FCSTD DOCUMENT  (FreeCAD 0.18R15611 (Git))
Label: sqare140mm
License: All rights reserved
LicenseURL: http://en.wikipedia.org/wiki/All_rights_reserved
objects: Sketcher::SketchObject×1, PartDesign::Pad×1, PartDesign::Body×1
note: 4 computed .brp shape members not serialized (recipe doc carries the construction recipe); baked Part::Feature solids carry a one-line shape summary decoded from their .brp

FEATURE [Sketcher::SketchObject] Sketch
  MapMode = 5
  Support = -> [XY_Plane]
  sketch-geometry (8):
    g0: LineSegment StartX=9.99983 StartY=10 StartZ=0 EndX=-10.0002 EndY=10 EndZ=0
    g1: LineSegment StartX=-10.0002 StartY=10 StartZ=0 EndX=-10.0002 EndY=-10 EndZ=0
    g2: LineSegment StartX=-10.0002 StartY=-10 StartZ=0 EndX=9.99983 EndY=-10 EndZ=0
    g3: LineSegment StartX=9.99983 StartY=-10 StartZ=0 EndX=9.99983 EndY=10 EndZ=0
    g4: LineSegment StartX=-8.5 StartY=-8.5 StartZ=0 EndX=8.5 EndY=-8.5 EndZ=0
    g5: LineSegment StartX=8.5 StartY=-8.5 StartZ=0 EndX=8.5 EndY=8.5 EndZ=0
    g6: LineSegment StartX=8.5 StartY=8.5 StartZ=0 EndX=-8.5 EndY=8.5 EndZ=0
    g7: LineSegment StartX=-8.5 StartY=8.5 StartZ=0 EndX=-8.5 EndY=-8.5 EndZ=0
  constraints (18):
    c: Coincident(g0,g1)
    c: Coincident(g1,g2)
    c: Coincident(g2,g3)
    c: Coincident(g3,g0)
    c: Horizontal(g0)
    c: Horizontal(g2)
    c: Vertical(g1)
    c: Vertical(g3)
    c: Coincident(g4,g5)
    c: Coincident(g5,g6)
    c: Coincident(g6,g7)
    c: Coincident(g7,g4)
    c: Horizontal(g4)
    c: Horizontal(g6)
    c: Vertical(g5)
    c: Vertical(g7)
    c: DistanceY(g2,g0) = 20
    c: DistanceY(g4,g5) = 17
FEATURE [PartDesign::Pad] Pad
  Length = 140
  Length2 = 100
  Profile = -> Sketch
  Type = 0
FEATURE [PartDesign::Body] Body
  Group = -> [Sketch,Pad]
  Origin = -> Origin
